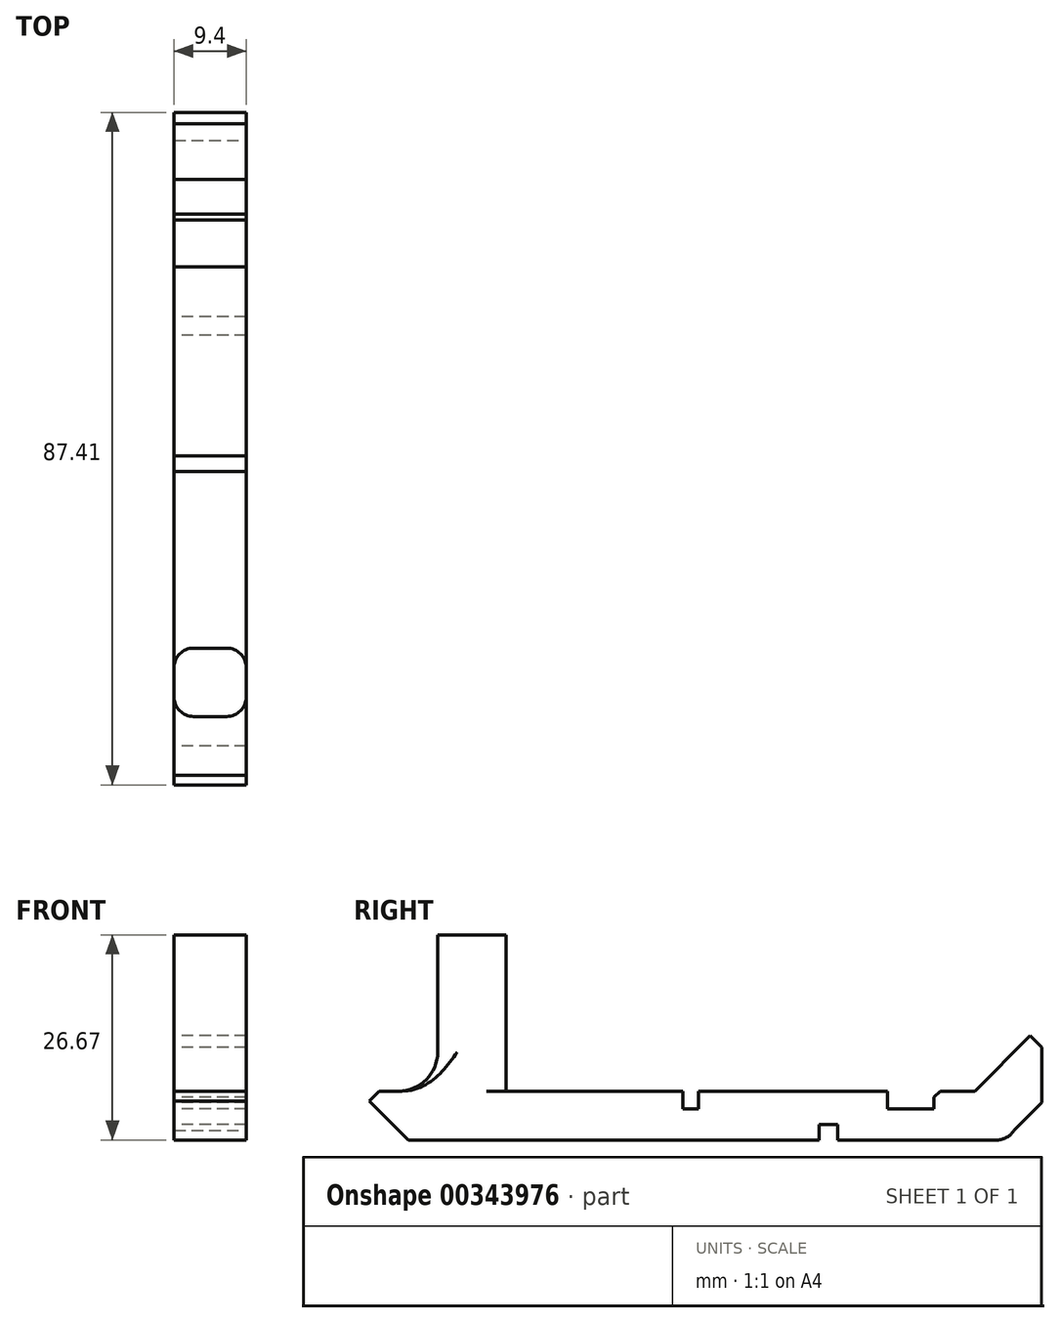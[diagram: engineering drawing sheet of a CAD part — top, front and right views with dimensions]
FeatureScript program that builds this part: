
annotation { "Feature Type Name" : "Feature", "Feature Type Description" : "" }
export const myFeature = defineFeature(function(context is Context, id is Id, definition is map)
    precondition{}
    {
        {
            var Q0;
            Q0=qCreatedBy(makeId("Top.planeOp"),FACE);
            var sketch = newSketch(context, id + "F0", { "sketchPlane" : qUnion([Q0])});
            skLineSegment(sketch, "E0.bottom", {"start": v(4.7, 41.91) * mm, "end": v(-4.7, 41.91) * mm});
            skLineSegment(sketch, "E0.top", {"start": v(4.7, -41.91) * mm, "end": v(-4.7, -41.91) * mm});
            skLineSegment(sketch, "E0.left", {"start": v(4.7, 41.91) * mm, "end": v(4.7, -41.91) * mm});
            skLineSegment(sketch, "E0.right", {"start": v(-4.7, 41.91) * mm, "end": v(-4.7, -41.91) * mm});
            skPoint(sketch, "E0.middle", {"position": v(0, 0) * mm});
            skSolve(sketch);
        }
        {
            var Q0;
            Q0=makeQuery(id+"F0.imprint","IMPRINT",FACE,{"disambiguationData":[TD([[makeQuery(id+"F0.imprint","IMPRINT",EDGE,{"derivedFrom":sQuery(id+"F0.wireOp",EDGE,"E0.bottom")}),1.0]])]});
            extrude(context, id + "F1", {"entities" : qUnion([Q0]), "depth" : 6.35 * mm});
        }
        {
            var Q0;
            Q0=makeQuery(id+"F1.opExtrude","CAP_FACE",FACE,{"disambiguationData":[OSD([sQuery(id+"F0.wireOp",EDGE,"E0.bottom"),sQuery(id+"F0.wireOp",EDGE,"E0.top"),sQuery(id+"F0.wireOp",EDGE,"E0.left"),sQuery(id+"F0.wireOp",EDGE,"E0.right")])],"isStart":true});
            var sketch = newSketch(context, id + "F2", { "sketchPlane" : qUnion([Q0])});
            skPoint(sketch, "E1", {"position": v(-4.7, -17.78) * mm});
            skPoint(sketch, "E2", {"position": v(4.7, -17.78) * mm});
            skLineSegment(sketch, "E3", {"start": v(4.7, -17.78) * mm, "end": v(-4.7, -17.78) * mm});
            skPoint(sketch, "E4", {"position": v(0, -17.78) * mm});
            skLineSegment(sketch, "E5.bottom", {"start": v(4.7, -18.99) * mm, "end": v(-4.7, -18.99) * mm});
            skLineSegment(sketch, "E5.top", {"start": v(4.7, -16.57) * mm, "end": v(-4.7, -16.57) * mm});
            skLineSegment(sketch, "E5.left", {"start": v(4.7, -18.99) * mm, "end": v(4.7, -16.57) * mm});
            skLineSegment(sketch, "E5.right", {"start": v(-4.7, -18.99) * mm, "end": v(-4.7, -16.57) * mm});
            skSolve(sketch);
        }
        {
            var Q0;
            {var subQ0=sQuery(id+"F2.wireOp",EDGE,"E3");Q0=makeQuery(id+"F2.imprint","IMPRINT",FACE,{"disambiguationData":[TD([[makeQuery(id+"F2.imprint","IMPRINT",EDGE,{"derivedFrom":subQ0}),1.0]])]});}
            var Q1;
            {var subQ0=sQuery(id+"F2.wireOp",EDGE,"E3");Q1=makeQuery(id+"F2.imprint","IMPRINT",FACE,{"disambiguationData":[TD([[makeQuery(id+"F2.imprint","IMPRINT",EDGE,{"derivedFrom":subQ0}),-1.0]])]});}
            extrude(context, id + "F3", {"entities" : qUnion([Q0, Q1]), "operationType" : NewBodyOperationType.REMOVE, "oppositeDirection" : true, "depth" : 2.03 * mm});
        }
        {
            var Q0;
            Q0=makeQuery(id+"F1.opExtrude","CAP_FACE",FACE,{"disambiguationData":[OSD([sQuery(id+"F0.wireOp",EDGE,"E0.bottom"),sQuery(id+"F0.wireOp",EDGE,"E0.top"),sQuery(id+"F0.wireOp",EDGE,"E0.left"),sQuery(id+"F0.wireOp",EDGE,"E0.right")])],"isStart":false});
            var sketch = newSketch(context, id + "F4", { "sketchPlane" : qUnion([Q0])});
            skPoint(sketch, "E6", {"position": v(4.7, -0.13) * mm});
            skPoint(sketch, "E7", {"position": v(-4.7, -0.13) * mm});
            skLineSegment(sketch, "E8", {"start": v(4.7, -0.13) * mm, "end": v(-4.7, -0.13) * mm});
            skPoint(sketch, "E9", {"position": v(0, -0.13) * mm});
            skLineSegment(sketch, "E10.bottom", {"start": v(4.7, 0.89) * mm, "end": v(-4.7, 0.89) * mm});
            skLineSegment(sketch, "E10.top", {"start": v(4.7, -1.14) * mm, "end": v(-4.7, -1.14) * mm});
            skLineSegment(sketch, "E10.left", {"start": v(4.7, 0.89) * mm, "end": v(4.7, -1.14) * mm});
            skLineSegment(sketch, "E10.right", {"start": v(-4.7, 0.89) * mm, "end": v(-4.7, -1.14) * mm});
            skSolve(sketch);
        }
        {
            var Q0;
            {var subQ0=sQuery(id+"F4.wireOp",EDGE,"E8");Q0=makeQuery(id+"F4.imprint","IMPRINT",FACE,{"disambiguationData":[TD([[makeQuery(id+"F4.imprint","IMPRINT",EDGE,{"derivedFrom":subQ0}),1.0]])]});}
            var Q1;
            {var subQ0=sQuery(id+"F4.wireOp",EDGE,"E8");Q1=makeQuery(id+"F4.imprint","IMPRINT",FACE,{"disambiguationData":[TD([[makeQuery(id+"F4.imprint","IMPRINT",EDGE,{"derivedFrom":subQ0}),-1.0]])]});}
            extrude(context, id + "F5", {"entities" : qUnion([Q0, Q1]), "operationType" : NewBodyOperationType.REMOVE, "oppositeDirection" : true, "depth" : 2.3 * mm});
        }
        {
            var Q0;
            {var subQ0=sQuery(id+"F0.wireOp",EDGE,"E0.top");var subQ1=sQuery(id+"F0.wireOp",EDGE,"E0.left");var subQ2=sQuery(id+"F0.wireOp",EDGE,"E0.right");Q0=makeQuery(id+"F5.boolean.opBoolean","SPLIT",FACE,{"disambiguationData":[TD([makeQuery(id+"F1.opExtrude","SWEPT_FACE",FACE,{"disambiguationData":[OSD([subQ0])]})])],"derivedFrom":makeQuery(id+"F1.opExtrude","CAP_FACE",FACE,{"disambiguationData":[OSD([sQuery(id+"F0.wireOp",EDGE,"E0.bottom"),subQ0,subQ1,subQ2])],"isStart":false})});}
            var sketch = newSketch(context, id + "F6", { "sketchPlane" : qUnion([Q0])});
            skLineSegment(sketch, "E11.bottom", {"start": v(4.7, -24.13) * mm, "end": v(-4.7, -24.13) * mm});
            skLineSegment(sketch, "E11.top", {"start": v(4.7, -33.02) * mm, "end": v(-4.7, -33.02) * mm});
            skLineSegment(sketch, "E11.left", {"start": v(4.7, -24.13) * mm, "end": v(4.7, -33.02) * mm});
            skLineSegment(sketch, "E11.right", {"start": v(-4.7, -24.13) * mm, "end": v(-4.7, -33.02) * mm});
            skSolve(sketch);
        }
        {
            var Q0;
            Q0=makeQuery(id+"F6.imprint","IMPRINT",FACE,{"disambiguationData":[TD([[makeQuery(id+"F6.imprint","IMPRINT",EDGE,{"derivedFrom":sQuery(id+"F6.wireOp",EDGE,"E11.bottom")}),1.0]])]});
            extrude(context, id + "F7", {"entities" : qUnion([Q0]), "operationType" : NewBodyOperationType.ADD, "depth" : 20.32 * mm});
        }
        {
            var Q0;
            Q0=makeQuery(id+"F7.opExtrude","SWEPT_EDGE",EDGE,{"disambiguationData":[OSD([sQuery(id+"F0.wireOp",EDGE,"E0.right"),sQuery(id+"F6.wireOp",EDGE,"E11.bottom"),sQuery(id+"F6.wireOp",EDGE,"E11.right")])]});
            var Q1;
            Q1=makeQuery(id+"F7.opExtrude","SWEPT_EDGE",EDGE,{"disambiguationData":[OSD([sQuery(id+"F0.wireOp",EDGE,"E0.right"),sQuery(id+"F6.wireOp",EDGE,"E11.top"),sQuery(id+"F6.wireOp",EDGE,"E11.right")])]});
            var Q2;
            Q2=makeQuery(id+"F7.opExtrude","SWEPT_EDGE",EDGE,{"disambiguationData":[OSD([sQuery(id+"F0.wireOp",EDGE,"E0.left"),sQuery(id+"F6.wireOp",EDGE,"E11.top"),sQuery(id+"F6.wireOp",EDGE,"E11.left")])]});
            var Q3;
            Q3=makeQuery(id+"F7.opExtrude","SWEPT_EDGE",EDGE,{"disambiguationData":[OSD([sQuery(id+"F0.wireOp",EDGE,"E0.left"),sQuery(id+"F6.wireOp",EDGE,"E11.bottom"),sQuery(id+"F6.wireOp",EDGE,"E11.left")])]});
            fillet(context, id + "F8", {"entities" : qUnion([Q0, Q1, Q2, Q3]), "radius" : 2.54 * mm, "tangentPropagation" : true, "allowEdgeOverflow" : false});
        }
        {
            var Q0;
            Q0=makeQuery(id+"F1.opExtrude","CAP_EDGE",EDGE,{"disambiguationData":[OSD([sQuery(id+"F0.wireOp",EDGE,"E0.top")])],"isStart":true});
            var Q1;
            Q1=makeQuery(id+"F1.opExtrude","CAP_EDGE",EDGE,{"disambiguationData":[OSD([sQuery(id+"F0.wireOp",EDGE,"E0.bottom")])],"isStart":false});
            chamfer(context, id + "F9", {"entities" : qUnion([Q0, Q1]), "width" : 5.08 * mm, "tangentPropagation" : true});
        }
        {
            var Q0;
            Q0=makeQuery(id+"F9.opChamfer","BLEND_FACE",FACE,{"disambiguationData":[OSD([sQuery(id+"F0.wireOp",EDGE,"E0.bottom")])]});
            extrude(context, id + "F10", {"entities" : qUnion([Q0]), "operationType" : NewBodyOperationType.ADD, "depth" : 10.16 * mm});
        }
        {
            var Q0;
            {var subQ0=sQuery(id+"F6.wireOp",EDGE,"E11.right");var subQ1=sQuery(id+"F0.wireOp",EDGE,"E0.right");Q0=makeQuery(id+"F10.boolean.opBoolean","MERGE",FACE,{"derivedFrom":[makeQuery(id+"F7.boolean.opBoolean","MERGE",FACE,{"derivedFrom":[makeQuery(id+"F1.opExtrude","SWEPT_FACE",FACE,{"disambiguationData":[OSD([subQ1])]}),makeQuery(id+"F7.opExtrude","SWEPT_FACE",FACE,{"disambiguationData":[OSD([subQ0])]})]}),makeQuery(id+"F10.opExtrude","SWEPT_FACE",FACE,{"disambiguationData":[OSD([sQuery(id+"F0.wireOp",EDGE,"E0.bottom"),subQ1,subQ0])]})]});}
            var sketch = newSketch(context, id + "F11", { "sketchPlane" : qUnion([Q0])});
            skLineSegment(sketch, "E12", {"start": v(-45.5, 12.05) * mm, "end": v(-45.5, 4.86) * mm});
            skPoint(sketch, "E12.startSnap0", {"position": v(-45.5, 4.86) * mm});
            skSolve(sketch);
        }
        {
            var Q0;
            {var subQ0=sQuery(id+"F11.wireOp",EDGE,"E12");Q0=makeQuery(id+"F11.imprint","IMPRINT",FACE,{"disambiguationData":[TD([[makeQuery(id+"F11.imprint","IMPRINT",EDGE,{"derivedFrom":subQ0}),-1.0]])]});}
            extrude(context, id + "F12", {"entities" : qUnion([Q0]), "operationType" : NewBodyOperationType.REMOVE, "endBound" : BoundingType.THROUGH_ALL, "oppositeDirection" : true, "depth" : 25.4 * mm});
        }
        {
            var Q0;
            Q0=makeQuery(id+"F7.opExtrude","CAP_EDGE",EDGE,{"disambiguationData":[OSD([sQuery(id+"F6.wireOp",EDGE,"E11.top")])],"isStart":true});
            var Q1;
            Q1=makeQuery(id+"F7.opExtrude","CAP_EDGE",EDGE,{"disambiguationData":[OSD([sQuery(id+"F6.wireOp",EDGE,"E11.bottom")])],"isStart":true});
            fillet(context, id + "F13", {"entities" : qUnion([Q0, Q1]), "radius" : 5.08 * mm, "tangentPropagation" : true, "allowEdgeOverflow" : false});
        }
        {
            var Q0;
            {var subQ0=makeQuery(id+"F5.opExtrude","SWEPT_FACE",FACE,{"disambiguationData":[OSD([sQuery(id+"F4.wireOp",EDGE,"E10.top")])]});var subQ1=sQuery(id+"F0.wireOp",EDGE,"E0.right");var subQ3=sQuery(id+"F0.wireOp",EDGE,"E0.left");var subQ5=sQuery(id+"F0.wireOp",EDGE,"E0.top");Q0=makeQuery(id+"F7.boolean.opBoolean","SPLIT",FACE,{"disambiguationData":[TD([makeQuery(id+"F5.boolean.opBoolean","COPY",FACE,{"derivedFrom":subQ0})])],"derivedFrom":makeQuery(id+"F5.boolean.opBoolean","SPLIT",FACE,{"disambiguationData":[TD([makeQuery(id+"F1.opExtrude","SWEPT_FACE",FACE,{"disambiguationData":[OSD([subQ5])]})])],"derivedFrom":makeQuery(id+"F1.opExtrude","CAP_FACE",FACE,{"disambiguationData":[OSD([sQuery(id+"F0.wireOp",EDGE,"E0.bottom"),subQ5,subQ3,subQ1])],"isStart":false})})});}
            var sketch = newSketch(context, id + "F14", { "sketchPlane" : qUnion([Q0])});
            skPoint(sketch, "E13", {"position": v(-4.7, 31.53) * mm});
            skPoint(sketch, "E14", {"position": v(4.7, 31.53) * mm});
            skLineSegment(sketch, "E15.left", {"start": v(-4.7, 31.53) * mm, "end": v(-4.7, 31.53) * mm});
            skLineSegment(sketch, "E15.right", {"start": v(4.7, 31.53) * mm, "end": v(4.7, 31.53) * mm});
            skLineSegment(sketch, "E16.bottom", {"start": v(-4.7, 31.53) * mm, "end": v(4.7, 31.53) * mm});
            skLineSegment(sketch, "E16.top", {"start": v(-4.7, 25.44) * mm, "end": v(4.7, 25.44) * mm});
            skLineSegment(sketch, "E16.left", {"start": v(-4.7, 31.53) * mm, "end": v(-4.7, 25.44) * mm});
            skLineSegment(sketch, "E16.right", {"start": v(4.7, 31.53) * mm, "end": v(4.7, 25.44) * mm});
            skSolve(sketch);
        }
        {
            var Q0;
            Q0=makeQuery(id+"F14.imprint","IMPRINT",FACE,{"disambiguationData":[TD([[makeQuery(id+"F14.imprint","IMPRINT",EDGE,{"derivedFrom":sQuery(id+"F14.wireOp",EDGE,"E16.bottom")}),-1.0]])]});
            extrude(context, id + "F15", {"entities" : qUnion([Q0]), "operationType" : NewBodyOperationType.REMOVE, "oppositeDirection" : true, "depth" : 2.3 * mm});
        }
        {
            var Q0;
            {var subQ0=sQuery(id+"F0.wireOp",EDGE,"E0.left");var subQ1=sQuery(id+"F0.wireOp",EDGE,"E0.top");Q0=makeQuery(id+"FFRHQAMNZy2JR3d_1.boolean.opBoolean","MERGE",EDGE,{"derivedFrom":[makeQuery(id+"FVACM9SGJdt5nFN_1.boolean.opBoolean","MERGE",EDGE,{"derivedFrom":[makeQuery(id+"F1.opExtrude","CAP_EDGE",EDGE,{"disambiguationData":[OSD([subQ1])],"isStart":false}),makeQuery(id+"FVACM9SGJdt5nFN_1.opExtrude","SWEPT_EDGE",EDGE,{"disambiguationData":[OSD([subQ1,subQ0])]})]}),makeQuery(id+"FFRHQAMNZy2JR3d_1.opExtrude","SWEPT_EDGE",EDGE,{"disambiguationData":[OSD([subQ1,subQ0])]})]});}
            chamfer(context, id + "F16", {"entities" : qUnion([Q0]), "width" : 1.27 * mm, "tangentPropagation" : true});
        }
        {
            var Q0;
            Q0=makeQuery(id+"F15.boolean.opBoolean","COPY",EDGE,{"derivedFrom":makeQuery(id+"F15.opExtrude","CAP_EDGE",EDGE,{"disambiguationData":[OSD([sQuery(id+"F14.wireOp",EDGE,"E16.bottom")])],"isStart":true})});
            var Q1;
            Q1=makeQuery(id+"F15.boolean.opBoolean","COPY",EDGE,{"derivedFrom":makeQuery(id+"F15.opExtrude","CAP_EDGE",EDGE,{"disambiguationData":[OSD([sQuery(id+"F14.wireOp",EDGE,"E16.top")])],"isStart":true})});
            chamfer(context, id + "F17", {"entities" : qUnion([Q0, Q1]), "width" : 0.76 * mm, "tangentPropagation" : true});
        }
        {
            var Q0;
            Q0=makeQuery(id+"F1.opExtrude","CAP_EDGE",EDGE,{"disambiguationData":[OSD([sQuery(id+"F0.wireOp",EDGE,"E0.bottom")])],"isStart":true});
            fillet(context, id + "F18", {"entities" : qUnion([Q0]), "radius" : 2.54 * mm, "tangentPropagation" : true, "allowEdgeOverflow" : false});
        }
    });
